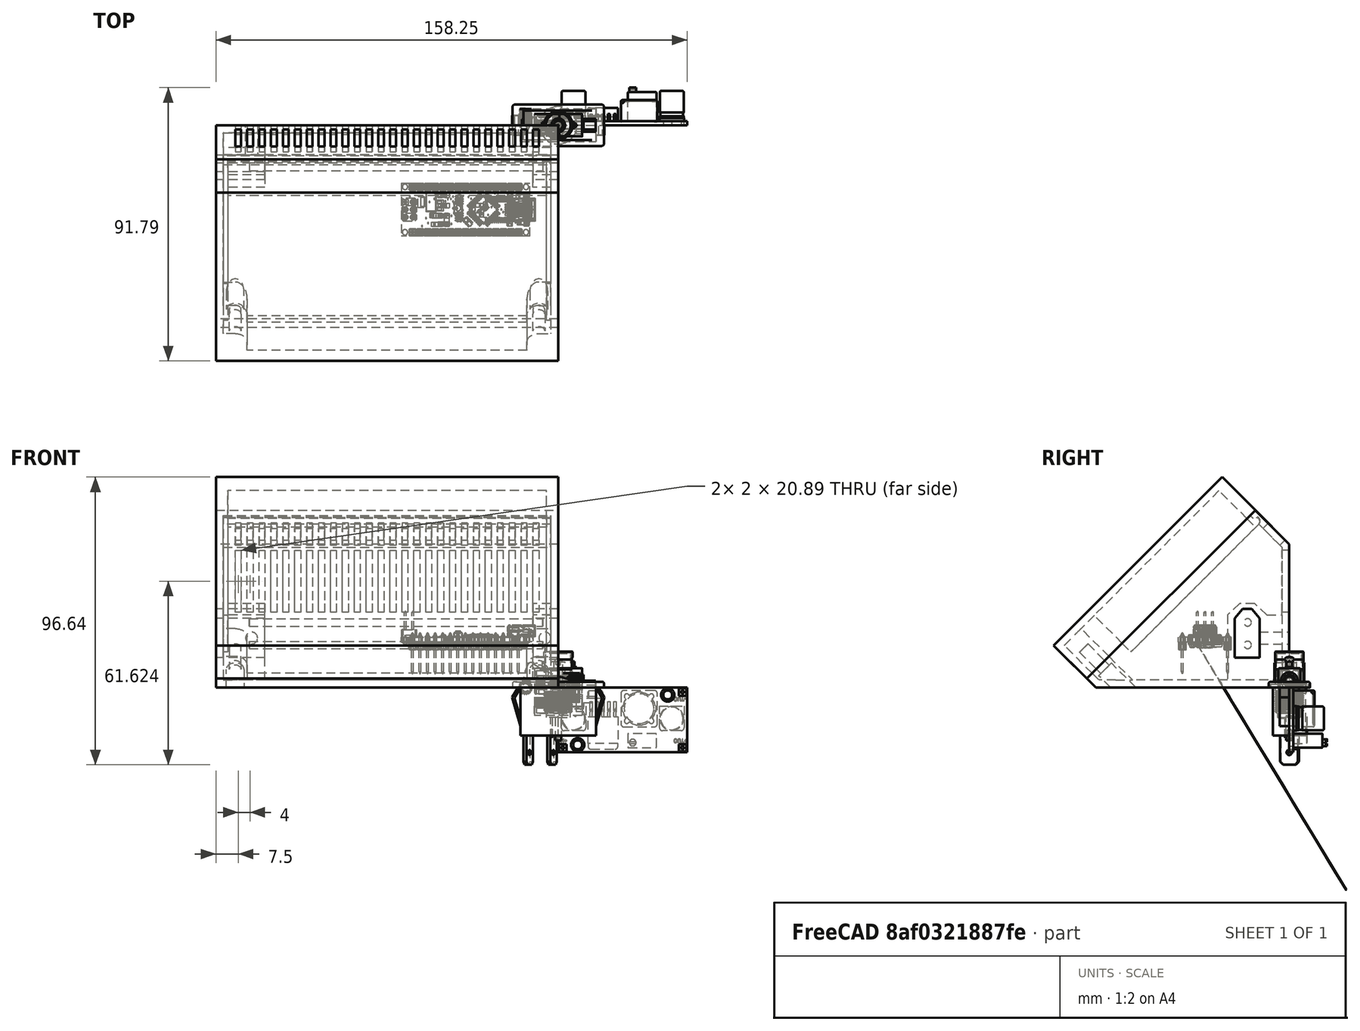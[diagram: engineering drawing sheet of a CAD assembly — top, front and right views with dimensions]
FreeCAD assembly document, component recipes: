
FREECAD ASSEMBLY — COMPONENT RECIPES ("genFonc_005_surBase35mm_008.1")

This assembly document has 17 components, labeled P0..P16 below (a component is one placed body or linked part). 10 of them carry a construction recipe — the FreeCAD feature program that regenerates the part from scratch, quoted from this document or its linked companion documents; the rest are supplied as boundary geometry only. No exploded tour is included for this assembly.
COMPONENT P0 — recipe-attached ("base", modeled in this document).
Construction recipe (the document's own serialized feature program — sketch geometry with constraints, then the solid features built on it; lengths are millimeters unless a unit is written):

FEATURE [PartDesign::FeatureBase] Clone
  BaseFeature = -> Slice_child0
FEATURE [PartDesign::Thickness] Thickness
  Base = -> Clone [Face7]
  BaseFeature = -> Clone
  Intersection = false
  Join = 0
  Mode = 0
  Reversed = true
  SupportTransform = false
  Value = 2.5
  expr: Value = <<sp>>.epaisseurParois
FEATURE [PartDesign::Plane] DatumPlane001  label="planXt"
  AttachmentOffset = pos=(0,0,-2.5) rot=(0,0,1;0rad)
  Length = 110.737
  MapMode = 5
  Placement = pos=(-2.5,6e-16,-6e-16) rot=(0.57735,0.57735,0.57735;2.0944rad)
  ResizeMode = 0
  Support = -> [YZ_Plane002]
  Width = 102.305
  expr: .AttachmentOffset.Base.z = -<<sp>>.epaisseurParois
FEATURE [Sketcher::SketchObject] Sketch002  label="sk_renfortXt"
  FullyConstrained = true
  MapMode = 5
  Placement = pos=(-2.5,6e-16,-6e-16) rot=(0.57735,0.57735,0.57735;2.0944rad)
  Support = -> [DatumPlane001]
  expr: Constraints[13] = <<sp>>.xt60largeurFetiere
  expr: Constraints[16] = <<sp>>.xt60base
  expr: Constraints[14] = <<sp>>.xt60hauteur
  expr: Constraints[18] = .Constraints.dist
  expr: Constraints[34] = .Constraints.epRf
  expr: .Constraints.epRf = <<sp>>.xt60epRenfort
  expr: Constraints[15] = <<sp>>.xt60hauteurToit
  expr: Constraints[45] = <<sp>>.epaisseurParois
  expr: .Constraints.dist = <<sp>>.xt60distanceAngleBord
  expr: Constraints[31] = <<sp>>.epaisseurParois
  expr: Constraints[32] = .Constraints.epRf
  sketch-geometry (17):
    g0: LineSegment StartX=-18.3 StartY=10 StartZ=0 EndX=-18.3 EndY=23.25 EndZ=0
    g1: LineSegment StartX=-18.3 StartY=23.25 StartZ=0 EndX=-15.65 EndY=25.75 EndZ=0
    g2: LineSegment StartX=-15.65 StartY=25.75 StartZ=0 EndX=-12.65 EndY=25.75 EndZ=0
    g3: LineSegment StartX=-12.65 StartY=25.75 StartZ=0 EndX=-10 EndY=23.25 EndZ=0
    g4: LineSegment StartX=-10 StartY=23.25 StartZ=0 EndX=-10 EndY=10 EndZ=0
    g5: LineSegment StartX=-10 StartY=10 StartZ=0 EndX=-18.3 EndY=10 EndZ=0
    g6: LineSegment StartX=-14.15 StartY=10 StartZ=0 EndX=-14.15 EndY=25.75 EndZ=0
    g7: LineSegment StartX=-16.6431 StartY=28.25 StartZ=0 EndX=-20.8 EndY=24.3284 EndZ=0
    g8: LineSegment StartX=-20.8 StartY=24.3284 StartZ=0 EndX=-20.8 EndY=2.5 EndZ=0
    g9: LineSegment StartX=-20.8 StartY=2.5 StartZ=0 EndX=-7.5 EndY=2.5 EndZ=0
    g10: LineSegment StartX=-7.5 StartY=2.5 StartZ=0 EndX=-7.5 EndY=24.3284 EndZ=0
    g11: LineSegment StartX=-7.5 StartY=24.3284 StartZ=0 EndX=-11.6569 EndY=28.25 EndZ=0
    g12: LineSegment StartX=-11.6569 StartY=28.25 StartZ=0 EndX=-16.6431 EndY=28.25 EndZ=0
    g13: LineSegment StartX=-7.5 StartY=24.3284 StartZ=0 EndX=-2.5 EndY=24.3284 EndZ=0
    g14: LineSegment StartX=-2.5 StartY=24.3284 StartZ=0 EndX=-2.5 EndY=2.5 EndZ=0
    g15: LineSegment StartX=-2.5 StartY=2.5 StartZ=0 EndX=-7.5 EndY=2.5 EndZ=0
    g16: LineSegment StartX=-7.5 StartY=2.5 StartZ=0 EndX=-7.5 EndY=24.3284 EndZ=0
  constraints (46):
    c: Vertical(g0)
    c: Coincident(g0,g1)
    c: Coincident(g1,g2)
    c: Horizontal(g2)
    c: Coincident(g2,g3)
    c: Coincident(g3,g4)
    c: Vertical(g4)
    c: Coincident(g4,g5)
    c: Coincident(g5,g0)
    c: Horizontal(g5)
    c: Symmetric(g1,g2,g6)
    c: Equal(g0,g4)
    c: Symmetric(g0,g4,g6)
    c: DistanceX(g2,g2) = 3
    c: DistanceY(g4,g4) = 13.25
    c: DistanceY(g3,g2) = 2.5
    c: DistanceX(g5,g5) = 8.3
    c: DistanceX(g4,g-1) = 10  'dist'
    c: DistanceY(g-1,g4) = 10
    c: Coincident(g7,g8)
    c: Vertical(g8)
    c: Coincident(g8,g9)
    c: Horizontal(g9)
    c: Coincident(g9,g10)
    c: Coincident(g10,g11)
    c: Coincident(g11,g12)
    c: Coincident(g12,g7)
    c: Symmetric(g7,g10,g6)
    c: Symmetric(g7,g11,g6)
    c: Symmetric(g8,g9,g6)
    c: DistanceX(g8,g0) = 2.5  'epRf'
    c: DistanceY(g-1,g9) = 2.5
    c: Distance(g7,g1) = 2.5
    c: Parallel(g1,g7)
    c: DistanceY(g2,g11) = 2.5
    c: Coincident(g13,g14)
    c: Coincident(g14,g15)
    c: Coincident(g15,g16)
    c: Coincident(g16,g13)
    c: Horizontal(g13)
    c: Horizontal(g15)
    c: Vertical(g14)
    c: Vertical(g16)
    c: Coincident(g13,g11)
    c: Horizontal(g14,g9)
    c: DistanceX(g14,g-1) = 2.5
FEATURE [PartDesign::Pad] Pad001  label="renfortXt"
  AllowMultiFace = false
  BaseFeature = -> Thickness
  Direction = (1,1,1)
  Length = 110
  Length2 = 100
  Profile = -> Sketch002
  Reversed = true
  Type = 0
  expr: Length = <<sp>>.largeurModuleBase - 2 * <<sp>>.epaisseurParois
FEATURE [Sketcher::SketchObject] Sketch003  label="sk_trouXt"
  FullyConstrained = true
  MapMode = 5
  Placement = pos=(0,0,0) rot=(0.57735,0.57735,0.57735;2.0944rad)
  Support = -> [YZ_Plane002]
  expr: Constraints[14] = <<sp>>.xt60hauteur
  expr: .Constraints.dist = <<sp>>.xt60distanceAngleBord
  expr: Constraints[15] = <<sp>>.xt60hauteurToit + <<sp>>.xtJeu
  expr: Constraints[16] = <<sp>>.xt60largeurFetiere
  expr: Constraints[13] = <<sp>>.xt60base
  expr: Constraints[18] = .Constraints.dist
  sketch-geometry (7):
    g0: LineSegment StartX=-18.3 StartY=10 StartZ=0 EndX=-18.3 EndY=23.25 EndZ=0
    g1: LineSegment StartX=-18.3 StartY=23.25 StartZ=0 EndX=-15.65 EndY=26.35 EndZ=0
    g2: LineSegment StartX=-15.65 StartY=26.35 StartZ=0 EndX=-12.65 EndY=26.35 EndZ=0
    g3: LineSegment StartX=-12.65 StartY=26.35 StartZ=0 EndX=-10 EndY=23.25 EndZ=0
    g4: LineSegment StartX=-10 StartY=23.25 StartZ=0 EndX=-10 EndY=10 EndZ=0
    g5: LineSegment StartX=-10 StartY=10 StartZ=0 EndX=-18.3 EndY=10 EndZ=0
    g6: LineSegment StartX=-14.15 StartY=10 StartZ=0 EndX=-14.15 EndY=26.35 EndZ=0
  constraints (19):
    c: Vertical(g0)
    c: Coincident(g0,g1)
    c: Coincident(g1,g2)
    c: Horizontal(g2)
    c: Coincident(g2,g3)
    c: Coincident(g3,g4)
    c: Coincident(g4,g5)
    c: Coincident(g5,g0)
    c: Horizontal(g5)
    c: Symmetric(g1,g2,g6)
    c: Symmetric(g0,g3,g6)
    c: Vertical(g6)
    c: Symmetric(g0,g4,g6)
    c: DistanceX(g5,g5) = 8.3
    c: DistanceY(g4,g4) = 13.25
    c: DistanceY(g3,g2) = 3.1
    c: DistanceX(g2,g2) = 3
    c: DistanceX(g4,g-1) = 10  'dist'
    c: DistanceY(g-1,g4) = 10
FEATURE [PartDesign::Pocket] Pocket
  AllowMultiFace = false
  BaseFeature = -> Pad001
  Length = 115
  Length2 = 100
  Profile = -> Sketch003
  Type = 0
  expr: Length = <<sp>>.largeurModuleBase
FEATURE [PartDesign::Plane] DatumPlane002  label="planDecoupeRenfortXt"
  AttachmentOffset = pos=(0,0,2.5) rot=(0,0,1;0rad)
  Length = 161.762
  MapMode = 5
  Placement = pos=(0,-2.5,-6e-16) rot=(1,0,0;1.5708rad)
  ResizeMode = 0
  Support = -> [XZ_Plane002]
  Width = 106.331
  expr: .AttachmentOffset.Base.z = <<sp>>.epaisseurParois
FEATURE [Sketcher::SketchObject] Sketch004  label="sk_decoupRenfXt"
  FullyConstrained = true
  MapMode = 5
  Placement = pos=(0,-2.5,-6e-16) rot=(1,0,0;1.5708rad)
  Support = -> [DatumPlane002]
  expr: Constraints[8] = <<sp>>.epaisseurParois
  expr: Constraints[9] = <<sp>>.xt60distanceAngleBord + <<sp>>.xt60hauteur + <<sp>>.xt60hauteurToit + <<sp>>.xt60epRenfort
  expr: Constraints[10] = <<sp>>.xt60LongueurRenfortPetit + <<sp>>.epaisseurParois
  expr: Constraints[11] = <<sp>>.largeurModuleBase - (<<sp>>.xt60longueurRenfortGrand + <<sp>>.epaisseurParois)
  sketch-geometry (4):
    g0: LineSegment StartX=-98.5 StartY=28.25 StartZ=0 EndX=-8.5 EndY=28.25 EndZ=0
    g1: LineSegment StartX=-8.5 StartY=28.25 StartZ=0 EndX=-8.5 EndY=2.5 EndZ=0
    g2: LineSegment StartX=-8.5 StartY=2.5 StartZ=0 EndX=-98.5 EndY=2.5 EndZ=0
    g3: LineSegment StartX=-98.5 StartY=2.5 StartZ=0 EndX=-98.5 EndY=28.25 EndZ=0
  constraints (12):
    c: Coincident(g0,g1)
    c: Coincident(g1,g2)
    c: Coincident(g2,g3)
    c: Coincident(g3,g0)
    c: Horizontal(g0)
    c: Horizontal(g2)
    c: Vertical(g1)
    c: Vertical(g3)
    c: DistanceY(g-1,g1) = 2.5
    c: DistanceY(g-1,g0) = 28.25
    c: DistanceX(g1,g-1) = 8.5
    c: DistanceX(g2,g-1) = 98.5
FEATURE [PartDesign::Pocket] Pocket001  label="decoupeRenfXt"
  AllowMultiFace = false
  BaseFeature = -> Pocket
  Length = 23.3
  Length2 = 100
  Profile = -> Sketch004
  Reversed = true
  Type = 0
  expr: Length = <<sp>>.xt60distanceAngleBord + <<sp>>.xt60base + 2 * <<sp>>.xt60epRenfort
FEATURE [Sketcher::SketchObject] Sketch005  label="xt60PercagePostMale"
  FullyConstrained = true
  MapMode = 5
  Placement = pos=(0,0,0) rot=(1,0,0;1.5708rad)
  Support = -> [XZ_Plane002]
  expr: Constraints[0] = <<sp>>.insertDiamPercage
  expr: Constraints[1] = <<sp>>.insertDistanceTrouBordMale
  expr: Constraints[2] = <<sp>>.insertHauteur
  sketch-geometry (1):
    g0: Circle CenterX=-4.5 CenterY=16.625 CenterZ=0 NormalX=0 NormalY=0 NormalZ=1 AngleXU=0 Radius=2
  constraints (3):
    c: Diameter(g0) = 4
    c: DistanceX(g0,g-1) = 4.5
    c: DistanceY(g-1,g0) = 16.625
FEATURE [PartDesign::Pocket] Pocket002  label="insertXtMale"
  AllowMultiFace = false
  BaseFeature = -> Pocket001
  Length = 10
  Length2 = 100
  Profile = -> Sketch005
  Reversed = true
  Type = 0
  expr: Length = <<sp>>.insertProfondeurPercage
FEATURE [Sketcher::SketchObject] Sketch006  label="xt60PercagePostFem"
  FullyConstrained = true
  MapMode = 5
  Placement = pos=(0,0,0) rot=(1,0,0;1.5708rad)
  Support = -> [XZ_Plane002]
  expr: Constraints[0] = <<sp>>.insertDiamPercage
  expr: Constraints[1] = <<sp>>.insertDistanceTrouBordFem
  expr: Constraints[2] = <<sp>>.insertHauteur
  sketch-geometry (1):
    g0: Circle CenterX=-103 CenterY=16.625 CenterZ=0 NormalX=0 NormalY=0 NormalZ=1 AngleXU=0 Radius=2
  constraints (3):
    c: Diameter(g0) = 4
    c: DistanceX(g0,g-1) = 103
    c: DistanceY(g-1,g0) = 16.625
FEATURE [PartDesign::Pocket] Pocket003  label="insertXt60Fem"
  AllowMultiFace = false
  BaseFeature = -> Pocket002
  Length = 10
  Length2 = 100
  Profile = -> Sketch006
  Reversed = true
  Type = 0
  expr: Length = <<sp>>.insertProfondeurPercage
FEATURE [PartDesign::Plane] DatumPlane003
  AttachmentOffset = pos=(0,0,2.5) rot=(0,0,1;0rad)
  Length = 162.821
  MapMode = 2
  Placement = pos=(0,0,2.5) rot=(0,0,1;0rad)
  ResizeMode = 0
  Support = -> [XY_Plane002]
  Width = 115.821
  expr: .AttachmentOffset.Base.z = <<sp>>.epaisseurParois
FEATURE [PartDesign::Plane] DatumPlane004  label="planTrancheur"
  AttachmentOffset = pos=(0,0,71) rot=(-1,0,0;0.785398rad)
  Length = 166.517
  MapMode = 5
  Placement = pos=(0,-71,-1.58e-14) rot=(1,0,0;0.785398rad)
  ResizeMode = 0
  Support = -> [XZ_Plane002]
  Width = 152.077
  expr: .AttachmentOffset.Base.z = <<sp>>.planTrancheur
FEATURE [Sketcher::SketchObject] Sketch008
  FullyConstrained = true
  MapMode = 5
  Placement = pos=(0,-71,-2.13e-14) rot=(1,0,0;0.785398rad)
  Support = -> [DatumPlane004]
  expr: Constraints[1] = <<sp>>.insertFavDistAuZeroDuPLan
  expr: Constraints[13] = <<sp>>.epaisseurParois
  expr: Constraints[16] = <<sp>>.insertDiamPercage / 2 + <<sp>>.insertFAVMargeDist
  expr: .Constraints.dist = <<sp>>.epaisseurParois
  expr: Constraints[21] = <<sp>>.insertFAVDistBord
  expr: Constraints[22] = <<sp>>.largeurModuleBase - <<sp>>.epaisseurParois
  sketch-geometry (7):
    g0: LineSegment StartX=-2.5 StartY=4.24264 StartZ=0 EndX=-112.5 EndY=4.24264 EndZ=0
    g1: LineSegment StartX=-6.5 StartY=14.7426 StartZ=0 EndX=-2.5 EndY=14.7426 EndZ=0
    g2: LineSegment StartX=-2.5 StartY=14.7426 StartZ=0 EndX=-2.5 EndY=6.74264 EndZ=0
    g3: LineSegment StartX=-2.5 StartY=6.74264 StartZ=0 EndX=-10.5 EndY=6.74264 EndZ=0
    g4: LineSegment StartX=-10.5 StartY=6.74264 StartZ=0 EndX=-10.5 EndY=10.7426 EndZ=0
    g5: ArcOfCircle CenterX=-6.5 CenterY=10.7426 CenterZ=0 NormalX=0 NormalY=0 NormalZ=1 AngleXU=0 Radius=4 StartAngle=1.5708 EndAngle=3.14159
    g6: LineSegment StartX=-6.5 StartY=10.7426 StartZ=0 EndX=-6.5 EndY=6.74264 EndZ=0
  constraints (23):
    c: Horizontal(g0)
    c: DistanceY(g-1,g0) = 4.24264
    c: DistanceX(g0,g-1) = 2.5  'dist'
    c: Horizontal(g1)
    c: Coincident(g1,g2)
    c: Vertical(g2)
    c: Coincident(g2,g3)
    c: Horizontal(g3)
    c: Coincident(g3,g4)
    c: Vertical(g4)
    c: Vertical(g2,g0)
    c: Equal(g3,g2)
    c: Equal(g4,g1)
    c: DistanceY(g0,g2) = 2.5
    c: Coincident(g5,g4)
    c: Coincident(g5,g1)
    c: DistanceX(g5,g2) = 4
    c: Coincident(g6,g5)
    c: PointOnObject(g6,g3)
    c: Vertical(g6)
    c: Vertical(g5,g1)
    c: DistanceX(g3,g3) = 8
    c: DistanceX(g0,g-1) = 112.5
FEATURE [PartDesign::Pad] Pad003  label="padTrouFAVDroite"
  AllowMultiFace = false
  BaseFeature = -> Pocket003
  Direction = (1,1,1)
  Length = 10
  Length2 = 100
  Profile = -> Sketch008
  Reversed = true
  Type = 3
  UpToFace = -> DatumPlane003
FEATURE [Sketcher::SketchObject] Sketch009
  FullyConstrained = true
  MapMode = 5
  Placement = pos=(0,-71,-2.13e-14) rot=(1,0,0;0.785398rad)
  Support = -> [DatumPlane004]
  expr: .Constraints.larg = <<sp>>.insertFAVDistBord
  expr: Constraints[8] = .Constraints.larg
  expr: Constraints[11] = .Constraints.larg / 2
  expr: Constraints[12] = <<sp>>.largeurModuleBase
  expr: Constraints[13] = <<sp>>.insertFavDistAuZeroDuPLan
  expr: Constraints[14] = <<sp>>.epaisseurParois
  expr: Constraints[15] = <<sp>>.epaisseurParois
  sketch-geometry (6):
    g0: LineSegment StartX=-112.5 StartY=6.74264 StartZ=0 EndX=-104.5 EndY=6.74264 EndZ=0
    g1: LineSegment StartX=-104.5 StartY=6.74264 StartZ=0 EndX=-104.5 EndY=10.7426 EndZ=0
    g2: LineSegment StartX=-108.5 StartY=14.7426 StartZ=0 EndX=-112.5 EndY=14.7426 EndZ=0
    g3: LineSegment StartX=-112.5 StartY=14.7426 StartZ=0 EndX=-112.5 EndY=6.74264 EndZ=0
    g4: ArcOfCircle CenterX=-108.5 CenterY=10.7426 CenterZ=0 NormalX=0 NormalY=0 NormalZ=1 AngleXU=0 Radius=4 StartAngle=0 EndAngle=1.5708
    g5: GeomPoint X=-115 Y=4.24264 Z=0
  constraints (16):
    c: Coincident(g0,g1)
    c: Coincident(g2,g3)
    c: Coincident(g3,g0)
    c: Horizontal(g0)
    c: Horizontal(g2)
    c: Vertical(g1)
    c: Vertical(g3)
    c: DistanceX(g0,g0) = 8  'larg'
    c: DistanceY(g3,g3) = 8
    c: Tangent(g2,g4) = -1.5708
    c: Tangent(g1,g4) = -1.5708
    c: DistanceX(g0,g4) = 4
    c: DistanceX(g5,g-1) = 115
    c: DistanceY(g-1,g5) = 4.24264
    c: DistanceX(g5,g0) = 2.5
    c: DistanceY(g5,g0) = 2.5
FEATURE [PartDesign::Pad] Pad004  label="padTrouFavGauche"
  AllowMultiFace = false
  BaseFeature = -> Pad003
  Direction = (1,1,1)
  Length = 10
  Length2 = 100
  Profile = -> Sketch009
  Type = 3
  UpToFace = -> DatumPlane003 [Plane]
FEATURE [Sketcher::SketchObject] Sketch010
  FullyConstrained = true
  MapMode = 5
  Placement = pos=(0,-71,-2.13e-14) rot=(1,0,0;0.785398rad)
  Support = -> [DatumPlane004]
  expr: Constraints[0] = <<sp>>.insertFAVDistBord / 2 + <<sp>>.epaisseurParois
  expr: Constraints[1] = <<sp>>.insertFavDistAuZeroDuPLan + <<sp>>.epaisseurParois + <<sp>>.insertFAVDistBord / 2
  expr: Constraints[2] = <<sp>>.insertDiamPercage
  sketch-geometry (1):
    g0: Circle CenterX=-6.5 CenterY=10.7426 CenterZ=0 NormalX=0 NormalY=0 NormalZ=1 AngleXU=0 Radius=2
  constraints (3):
    c: DistanceX(g0,g-1) = 6.5
    c: DistanceY(g-1,g0) = 10.7426
    c: Diameter(g0) = 4
FEATURE [PartDesign::Pocket] Pocket004  label="trouDroit"
  AllowMultiFace = false
  BaseFeature = -> Pad004
  Length = 5
  Length2 = 100
  Profile = -> Sketch010
  Type = 1
FEATURE [Sketcher::SketchObject] Sketch011
  FullyConstrained = true
  MapMode = 5
  Placement = pos=(0,-71,-2.13e-14) rot=(1,0,0;0.785398rad)
  Support = -> [DatumPlane004]
  expr: Constraints[0] = <<sp>>.insertDiamPercage
  expr: Constraints[1] = <<sp>>.largeurModuleBase - <<sp>>.epaisseurParois - <<sp>>.insertFAVDistBord / 2
  expr: Constraints[2] = <<sp>>.insertFavDistAuZeroDuPLan + <<sp>>.epaisseurParois + <<sp>>.insertFAVDistBord / 2
  sketch-geometry (1):
    g0: Circle CenterX=-108.5 CenterY=10.7426 CenterZ=0 NormalX=0 NormalY=0 NormalZ=1 AngleXU=0 Radius=2
  constraints (3):
    c: Diameter(g0) = 4
    c: DistanceX(g0,g-1) = 108.5
    c: DistanceY(g-1,g0) = 10.7426
FEATURE [PartDesign::Pocket] Pocket005  label="trouGauche"
  AllowMultiFace = false
  BaseFeature = -> Pocket004
  Length = 5
  Length2 = 100
  Profile = -> Sketch011
  Type = 1
FEATURE [PartDesign::Plane] DatumPlane005  label="planTeteVisFav"
  AttachmentOffset = pos=(0,0,68) rot=(-1,0,0;0.785398rad)
  Length = 166.517
  MapMode = 5
  Placement = pos=(0,-68,-1.51e-14) rot=(1,0,0;0.785398rad)
  ResizeMode = 0
  Support = -> [XZ_Plane002]
  Width = 152.077
  expr: .AttachmentOffset.Base.z = <<sp>>.planTrancheur - 3
FEATURE [Sketcher::SketchObject] Sketch012
  ExternalGeometry = -> [Pocket005]
  FullyConstrained = true
  MapMode = 5
  Placement = pos=(0,-68,-1.42e-14) rot=(1,0,0;0.785398rad)
  Support = -> [DatumPlane005]
  expr: Constraints[1] = <<sp>>.visM3DiamEncastrement
  sketch-geometry (2):
    g0: Circle CenterX=-6.5 CenterY=8.62132 CenterZ=0 NormalX=0 NormalY=0 NormalZ=1 AngleXU=0 Radius=3
    g1: Circle CenterX=-108.5 CenterY=8.62132 CenterZ=0 NormalX=0 NormalY=0 NormalZ=1 AngleXU=0 Radius=3
  constraints (4):
    c: Equal(g0,g1)
    c: Diameter(g1) = 6
    c: Coincident(g1,g-4)
    c: Coincident(g-3,g0)
FEATURE [PartDesign::Pocket] Pocket006  label="evidementTeteVisFav"
  AllowMultiFace = false
  BaseFeature = -> Pocket005
  Length = 20
  Length2 = 100
  Profile = -> Sketch012
  Type = 1
FEATURE [Sketcher::SketchObject] Sketch014
  FullyConstrained = true
  MapMode = 5
  Placement = pos=(0,0,0) rot=(1,0,0;1.5708rad)
  Support = -> [XZ_Plane002]
  expr: Constraints[2] = <<sp>>.hauteurDuDos
  expr: Constraints[3] = <<sp>>.largeurModuleBase / 2
  expr: Constraints[12] = <<sp>>.xt60distanceAngleBord + <<sp>>.xt60hauteur + <<sp>>.ventilDistBordFente
  expr: Constraints[13] = <<sp>>.ventilLargeurFentes
  expr: Constraints[14] = <<sp>>.ventilEcartfente / 2
  expr: Constraints[15] = <<sp>>.hauteurDuDos - <<sp>>.ventilDistBordFente
  sketch-geometry (5):
    g0: LineSegment StartX=-57.5 StartY=0 StartZ=0 EndX=-57.5 EndY=48.1371 EndZ=0
    g1: LineSegment StartX=-60.5 StartY=46.1371 StartZ=0 EndX=-58.5 EndY=46.1371 EndZ=0
    g2: LineSegment StartX=-58.5 StartY=46.1371 StartZ=0 EndX=-58.5 EndY=25.25 EndZ=0
    g3: LineSegment StartX=-58.5 StartY=25.25 StartZ=0 EndX=-60.5 EndY=25.25 EndZ=0
    g4: LineSegment StartX=-60.5 StartY=25.25 StartZ=0 EndX=-60.5 EndY=46.1371 EndZ=0
  constraints (16):
    c: PointOnObject(g0,g-1)
    c: Vertical(g0)
    c: DistanceY(g0,g0) = 48.1371
    c: DistanceX(g0,g-1) = 57.5
    c: Coincident(g1,g2)
    c: Coincident(g2,g3)
    c: Coincident(g3,g4)
    c: Coincident(g4,g1)
    c: Horizontal(g1)
    c: Horizontal(g3)
    c: Vertical(g2)
    c: Vertical(g4)
    c: DistanceY(g-1,g2) = 25.25
    c: DistanceX(g1,g1) = 2
    c: DistanceX(g2,g0) = 1
    c: DistanceY(g-1,g1) = 46.1371
FEATURE [PartDesign::Pocket] Pocket008  label="ventilFente1"
  AllowMultiFace = false
  BaseFeature = -> Pocket006
  Length = 2.5
  Length2 = 100
  Profile = -> Sketch014
  Reversed = true
  Type = 0
  expr: Length = <<sp>>.epaisseurParois
FEATURE [PartDesign::LinearPattern] LinearPattern  label="ventilDosRepeat1"
  BaseFeature = -> Pocket008
  Direction = -> Sketch014 [H_Axis]
  Length = 48
  Occurrences = 13
  Originals = -> [Pocket008]
  Reversed = true
  expr: Length = <<sp>>.ventilLargeurRepet
  expr: Occurrences = <<sp>>.ventilNbrFents
FEATURE [PartDesign::LinearPattern] LinearPattern001  label="ventilDosRepeat2"
  BaseFeature = -> LinearPattern
  Direction = -> Sketch014 [H_Axis]
  Length = 52
  Occurrences = 14
  Originals = -> [Pocket008]
  expr: Length = <<sp>>.ventilLargeurRepet + <<sp>>.ventilEcartfente + <<sp>>.ventilLargeurFentes
  expr: Occurrences = <<sp>>.ventilNbrFents + 1
FEATURE [PartDesign::Plane] DatumPlane006  label="planVentilSup"
  AttachmentOffset = pos=(0,0,-48.1371) rot=(1,0,0;0.785398rad)
  Length = 166.517
  MapMode = 5
  Placement = pos=(0,48.1371,1.07e-14) rot=(1,0,0;2.35619rad)
  ResizeMode = 0
  Support = -> [XZ_Plane002]
  Width = 152.077
  expr: .AttachmentOffset.Base.z = -<<sp>>.hauteurDuDos
FEATURE [Sketcher::SketchObject] Sketch015
  FullyConstrained = true
  MapMode = 5
  Placement = pos=(0,48.1371,1.07e-14) rot=(1,0,0;2.35619rad)
  Support = -> [DatumPlane006]
  expr: Constraints[8] = <<sp>>.distanceAuZeroPlanBorArriere + <<sp>>.ventilDistBordFente
  expr: Constraints[10] = <<sp>>.ventilLargeurFentes
  expr: Constraints[11] = (<<sp>>.largeurModuleBase + <<sp>>.ventilEcartfente) / 2
  expr: Constraints[9] = <<sp>>.longPetitRetSupSansFav - 2 * <<sp>>.ventilDistBordFente - <<sp>>.favBordureProf
  sketch-geometry (4):
    g0: LineSegment StartX=-58.5 StartY=78.0926 StartZ=0 EndX=-60.5 EndY=78.0926 EndZ=0
    g1: LineSegment StartX=-60.5 StartY=78.0926 StartZ=0 EndX=-60.5 EndY=70.0761 EndZ=0
    g2: LineSegment StartX=-60.5 StartY=70.0761 StartZ=0 EndX=-58.5 EndY=70.0761 EndZ=0
    g3: LineSegment StartX=-58.5 StartY=70.0761 StartZ=0 EndX=-58.5 EndY=78.0926 EndZ=0
  constraints (12):
    c: Coincident(g0,g1)
    c: Coincident(g1,g2)
    c: Coincident(g2,g3)
    c: Coincident(g3,g0)
    c: Horizontal(g0)
    c: Horizontal(g2)
    c: Vertical(g1)
    c: Vertical(g3)
    c: DistanceY(g-1,g2) = 70.0761
    c: DistanceY(g2,g0) = 8.01652
    c: DistanceX(g0,g0) = 2
    c: DistanceX(g2,g-1) = 58.5
FEATURE [PartDesign::Pocket] Pocket009  label="ventilSupFente"
  AllowMultiFace = false
  BaseFeature = -> LinearPattern001
  Length = 5
  Length2 = 100
  Profile = -> Sketch015
  Reversed = true
  Type = 0
FEATURE [PartDesign::LinearPattern] LinearPattern002  label="ventilSupRepeat1"
  BaseFeature = -> Pocket009
  Direction = -> Sketch015 [H_Axis]
  Length = 48
  Occurrences = 13
  Originals = -> [Pocket009]
  Reversed = true
  expr: Length = <<sp>>.ventilLargeurRepet
  expr: Occurrences = <<sp>>.ventilNbrFents
FEATURE [PartDesign::LinearPattern] LinearPattern003  label="ventilSupRepeat2"
  BaseFeature = -> LinearPattern002
  Direction = -> Sketch015 [H_Axis]
  Length = 52
  Occurrences = 14
  Originals = -> [Pocket009]
  expr: Length = <<sp>>.ventilLargeurRepet + <<sp>>.ventilEcartfente + <<sp>>.ventilLargeurFentes
  expr: Occurrences = <<sp>>.ventilNbrFents + 1
FEATURE [PartDesign::Body] Body001  label="base"
  BaseFeature = -> Slice_child0
  Group = -> [Clone,Thickness,DatumPlane001,Sketch002,Pad001,Sketch003,Pocket,DatumPlane002,Sketch004,Pocket001,Sketch005,Pocket002,Sketch006,Pocket003,DatumPlane003,DatumPlane004,Sketch008,Pad003,Sketch009,Pad004,Sketch010,Pocket004,Sketch011,Pocket005,DatumPlane005,Sketch012,Pocket006,Sketch014,Pocket008,LinearPattern,LinearPattern001,DatumPlane006,Sketch015,Pocket009,LinearPattern002,LinearPattern003,+3 more]
  Origin = -> Origin002
  Tip = -> Pocket015
COMPONENT P1 — recipe-attached ("faceAvant", modeled in this document).
Construction recipe (the document's own serialized feature program — sketch geometry with constraints, then the solid features built on it; lengths are millimeters unless a unit is written):

FEATURE [PartDesign::FeatureBase] Clone001
  BaseFeature = -> Slice_child1
FEATURE [PartDesign::Thickness] Thickness001
  Base = -> Clone001 [Face5]
  BaseFeature = -> Clone001
  Intersection = false
  Join = 0
  Mode = 0
  Reversed = true
  SupportTransform = false
  Value = 2.5
  expr: Value = <<sp>>.epaisseurParois
FEATURE [PartDesign::Plane] DatumPlane007  label="planTrancheurBis"
  AttachmentOffset = pos=(0,0,71) rot=(-1,0,0;0.785398rad)
  Length = 168.138
  MapMode = 5
  Placement = pos=(0,-71,-1.58e-14) rot=(1,0,0;0.785398rad)
  ResizeMode = 0
  Support = -> [XZ_Plane003]
  Width = 169.523
  expr: .AttachmentOffset.Base.z = <<sp>>.planTrancheur
FEATURE [Sketcher::SketchObject] Sketch016  label="sk_insertFavDroit"
  FullyConstrained = true
  MapMode = 5
  Placement = pos=(0,-71,-2.13e-14) rot=(1,0,0;0.785398rad)
  Support = -> [DatumPlane007]
  expr: Constraints[7] = <<sp>>.epaisseurParois
  expr: Constraints[8] = <<sp>>.insertFavDistAuZeroDuPLan + <<sp>>.epaisseurParois
  expr: Constraints[9] = <<sp>>.insertFAVDistBord
  expr: Constraints[14] = <<sp>>.insertFAVDistBord / 2
  expr: Constraints[11] = <<sp>>.insertFAVDistBord
  sketch-geometry (5):
    g0: LineSegment StartX=-6.5 StartY=14.7426 StartZ=0 EndX=-2.5 EndY=14.7426 EndZ=0
    g1: LineSegment StartX=-2.5 StartY=14.7426 StartZ=0 EndX=-2.5 EndY=6.74264 EndZ=0
    g2: LineSegment StartX=-2.5 StartY=6.74264 StartZ=0 EndX=-10.5 EndY=6.74264 EndZ=0
    g3: LineSegment StartX=-10.5 StartY=6.74264 StartZ=0 EndX=-10.5 EndY=10.7426 EndZ=0
    g4: ArcOfCircle CenterX=-6.5 CenterY=10.7426 CenterZ=0 NormalX=0 NormalY=0 NormalZ=1 AngleXU=0 Radius=4 StartAngle=1.5708 EndAngle=3.14159
  constraints (15):
    c: Horizontal(g0)
    c: Coincident(g0,g1)
    c: Vertical(g1)
    c: Coincident(g1,g2)
    c: Horizontal(g2)
    c: Coincident(g2,g3)
    c: Vertical(g3)
    c: DistanceX(g1,g-1) = 2.5
    c: DistanceY(g-1,g1) = 6.74264
    c: DistanceY(g1,g1) = 8
    c: Equal(g3,g0)
    c: DistanceX(g2,g2) = 8
    c: Coincident(g4,g0)
    c: Tangent(g4,g3) = 1.5708
    c: DistanceX(g4,g1) = 4
FEATURE [PartDesign::Pad] Pad005  label="padInsertFavDroit"
  AllowMultiFace = false
  BaseFeature = -> Thickness001
  Direction = (1,1,1)
  Length = 10
  Length2 = 100
  Profile = -> Sketch016
  Type = 2
FEATURE [Sketcher::SketchObject] Sketch017  label="sp_padInserFavGauch"
  FullyConstrained = true
  MapMode = 5
  Placement = pos=(0,-71,-2.13e-14) rot=(1,0,0;0.785398rad)
  Support = -> [DatumPlane007]
  expr: Constraints[12] = <<sp>>.insertFAVDistBord / 2
  expr: Constraints[10] = <<sp>>.insertFAVDistBord
  expr: Constraints[13] = <<sp>>.largeurModuleBase
  expr: Constraints[14] = <<sp>>.insertFavDistAuZeroDuPLan
  expr: Constraints[15] = <<sp>>.epaisseurParois
  expr: Constraints[16] = <<sp>>.epaisseurParois
  sketch-geometry (6):
    g0: LineSegment StartX=-108.5 StartY=14.7426 StartZ=0 EndX=-112.5 EndY=14.7426 EndZ=0
    g1: LineSegment StartX=-112.5 StartY=14.7426 StartZ=0 EndX=-112.5 EndY=6.74264 EndZ=0
    g2: LineSegment StartX=-112.5 StartY=6.74264 StartZ=0 EndX=-104.5 EndY=6.74264 EndZ=0
    g3: LineSegment StartX=-104.5 StartY=6.74264 StartZ=0 EndX=-104.5 EndY=10.7426 EndZ=0
    g4: ArcOfCircle CenterX=-108.5 CenterY=10.7426 CenterZ=0 NormalX=0 NormalY=0 NormalZ=1 AngleXU=0 Radius=4 StartAngle=2e-16 EndAngle=1.5708
    g5: GeomPoint X=-115 Y=4.24264 Z=0
  constraints (17):
    c: Horizontal(g0)
    c: Coincident(g0,g1)
    c: Vertical(g1)
    c: Coincident(g1,g2)
    c: Horizontal(g2)
    c: Coincident(g2,g3)
    c: Vertical(g3)
    c: Equal(g3,g0)
    c: Equal(g2,g1)
    c: Coincident(g0,g4)
    c: DistanceX(g2,g2) = 8
    c: Tangent(g4,g3) = -1.5708
    c: DistanceX(g0,g0) = 4
    c: DistanceX(g5,g-1) = 115
    c: DistanceY(g-1,g5) = 4.24264
    c: DistanceY(g5,g1) = 2.5
    c: DistanceX(g5,g1) = 2.5
FEATURE [PartDesign::Pad] Pad006  label="padInsertFavGauch"
  AllowMultiFace = false
  BaseFeature = -> Pad005
  Direction = (1,1,1)
  Length = 10
  Length2 = 100
  Profile = -> Sketch017
  Type = 2
FEATURE [Sketcher::SketchObject] Sketch018  label="skPercageInsertFavDroit"
  FullyConstrained = true
  MapMode = 5
  Placement = pos=(0,-71,-2.13e-14) rot=(1,0,0;0.785398rad)
  Support = -> [DatumPlane007]
  expr: Constraints[0] = <<sp>>.insertDiamPercage
  expr: Constraints[1] = <<sp>>.insertFavDistAuZeroDuPLan + <<sp>>.epaisseurParois + <<sp>>.insertFAVDistBord / 2
  expr: Constraints[2] = <<sp>>.epaisseurParois + <<sp>>.insertFAVDistBord / 2
  expr: Constraints[7] = <<sp>>.largeurModuleBase - 2 * <<sp>>.epaisseurParois - <<sp>>.insertFAVDistBord
  sketch-geometry (3):
    g0: Circle CenterX=-6.5 CenterY=10.7426 CenterZ=0 NormalX=0 NormalY=0 NormalZ=1 AngleXU=0 Radius=2
    g1: Circle CenterX=-108.5 CenterY=10.7426 CenterZ=0 NormalX=0 NormalY=0 NormalZ=1 AngleXU=0 Radius=2
    g2: LineSegment StartX=-108.5 StartY=10.7426 StartZ=0 EndX=-6.5 EndY=10.7426 EndZ=0
  constraints (8):
    c: Diameter(g0) = 4
    c: DistanceY(g-1,g0) = 10.7426
    c: DistanceX(g0,g-1) = 6.5
    c: Equal(g0,g1)
    c: Coincident(g2,g1)
    c: Coincident(g2,g0)
    c: Horizontal(g2)
    c: DistanceX(g2,g2) = 102
FEATURE [PartDesign::Pocket] Pocket010  label="trouInsertFavDroit"
  AllowMultiFace = false
  BaseFeature = -> Pad006
  Length = 8
  Length2 = 100
  Profile = -> Sketch018
  Reversed = true
  Type = 0
  expr: Length = <<sp>>.insertFavProfondeur
FEATURE [PartDesign::Plane] DatumPlane011  label="planFaceAvant"
  AttachmentOffset = pos=(0,0,93.2843) rot=(-1,0,0;0.785398rad)
  Length = 168.138
  MapMode = 5
  Placement = pos=(0,-93.2843,-2.07e-14) rot=(1,0,0;0.785398rad)
  ResizeMode = 0
  Support = -> [XZ_Plane003]
  Width = 169.523
  expr: .AttachmentOffset.Base.z = <<sp>>.planFaceAvant
FEATURE [Sketcher::SketchObject] Sketch030  label="sk_rebordFav"
  FullyConstrained = true
  MapMode = 5
  Placement = pos=(0,-71,-2.13e-14) rot=(1,0,0;0.785398rad)
  Support = -> [DatumPlane007]
  expr: Constraints[0] = <<sp>>.insertFavDistAuZeroDuPLan
  expr: Constraints[20] = <<sp>>.favEpBordure
  expr: Constraints[24] = <<sp>>.Face - <<sp>>.epaisseurParois
  expr: Constraints[21] = <<sp>>.favDistBordPlan
  expr: Constraints[25] = <<sp>>.favEpBordure
  expr: Constraints[22] = <<sp>>.largeurModuleBase - 2 * <<sp>>.epaisseurParois
  expr: Constraints[19] = <<sp>>.epaisseurParois
  expr: Constraints[23] = <<sp>>.favEpBordure
  sketch-geometry (9):
    g0: GeomPoint X=0 Y=4.24264 Z=0
    g1: LineSegment StartX=-112.5 StartY=20.9853 StartZ=0 EndX=-112.5 EndY=81.7426 EndZ=0
    g2: LineSegment StartX=-112.5 StartY=81.7426 StartZ=0 EndX=-2.5 EndY=81.7426 EndZ=0
    g3: LineSegment StartX=-2.5 StartY=81.7426 StartZ=0 EndX=-2.5 EndY=20.9853 EndZ=0
    g4: LineSegment StartX=-2.5 StartY=20.9853 StartZ=0 EndX=-4 EndY=20.9853 EndZ=0
    g5: LineSegment StartX=-4 StartY=20.9853 StartZ=0 EndX=-4 EndY=80.2426 EndZ=0
    g6: LineSegment StartX=-4 StartY=80.2426 StartZ=0 EndX=-111 EndY=80.2426 EndZ=0
    g7: LineSegment StartX=-111 StartY=80.2426 StartZ=0 EndX=-111 EndY=20.9853 EndZ=0
    g8: LineSegment StartX=-111 StartY=20.9853 StartZ=0 EndX=-112.5 EndY=20.9853 EndZ=0
  constraints (26):
    c: DistanceY(g-1,g0) = 4.24264
    c: Vertical(g0,g-1)
    c: Vertical(g1)
    c: Coincident(g1,g2)
    c: Horizontal(g2)
    c: Coincident(g2,g3)
    c: Vertical(g3)
    c: Coincident(g3,g4)
    c: Horizontal(g4)
    c: Coincident(g4,g5)
    c: Vertical(g5)
    c: Coincident(g5,g6)
    c: Horizontal(g6)
    c: Coincident(g6,g7)
    c: Vertical(g7)
    c: Coincident(g7,g8)
    c: Coincident(g8,g1)
    c: Horizontal(g8)
    c: Horizontal(g7,g4)
    c: DistanceX(g3,g0) = 2.5
    c: DistanceX(g4,g4) = 1.5
    c: DistanceY(g0,g3) = 16.7426
    c: DistanceX(g1,g3) = 110
    c: DistanceY(g5,g2) = 1.5
    c: DistanceY(g0,g2) = 77.5
    c: DistanceX(g1,g7) = 1.5
FEATURE [PartDesign::Pad] Pad014  label="favRebordSupport"
  AllowMultiFace = false
  BaseFeature = -> Pocket010
  Direction = (1,1,1)
  Length = 10
  Length2 = 100
  Profile = -> Sketch030
  Type = 3
  UpToFace = -> Pocket010 [Face13]
FEATURE [PartDesign::Pad] Pad015  label="favRebord"
  AllowMultiFace = false
  BaseFeature = -> Pad014
  Direction = (1,1,1)
  Length = 4.15
  Length2 = 100
  Profile = -> Sketch030
  Reversed = true
  Type = 0
  expr: Length = <<sp>>.favBordureProf
FEATURE [Sketcher::SketchObject] Sketch031  label="sk_bourlet"
  ExternalGeometry = -> [Pad015]
  FullyConstrained = true
  MapMode = 5
  Placement = pos=(-2.5,0,0) rot=(0.57735,0.57735,0.57735;2.0944rad)
  Support = -> [Pad015]
  expr: Constraints[3] = <<sp>>.bourletMaintientRayon - <<sp>>.bourletRayonJeu
  sketch-geometry (2):
    g0: ArcOfCircle CenterX=-11.184 CenterY=55.7855 CenterZ=0 NormalX=0 NormalY=0 NormalZ=1 AngleXU=0 Radius=1.3 StartAngle=5.49779 EndAngle=8.63938
    g1: LineSegment StartX=-12.1032 StartY=56.7048 StartZ=0 EndX=-10.2647 EndY=54.8663 EndZ=0
  constraints (6):
    c: Coincident(g0,g-3)
    c: PointOnObject(g0,g-3)
    c: PointOnObject(g0,g-3)
    c: Radius(g0) = 1.3
    c: Coincident(g1,g0)
    c: Coincident(g1,g0)
FEATURE [PartDesign::Pad] Pad016  label="bourlet"
  AllowMultiFace = false
  BaseFeature = -> Pad015
  Direction = (1,1,1)
  Length = 10
  Length2 = 100
  Profile = -> Sketch031
  Reversed = true
  Type = 3
  UpToFace = -> Pad015 [Face11]
FEATURE [Sketcher::SketchObject] Sketch039
  FullyConstrained = false
  MapMode = 5
  Placement = pos=(0,-93.2843,-2.84e-14) rot=(1,0,0;0.785398rad)
  Support = -> [DatumPlane011]
  sketch-geometry (4):
    g0: LineSegment StartX=0 StartY=20.0821 StartZ=0 EndX=-90.3326 EndY=20.0821 EndZ=0
    g1: LineSegment StartX=-90.3326 StartY=20.0821 StartZ=0 EndX=-90.3326 EndY=100.134 EndZ=0
    g2: LineSegment StartX=-90.3326 StartY=100.134 StartZ=0 EndX=0 EndY=100.134 EndZ=0
    g3: LineSegment StartX=0 StartY=100.134 StartZ=0 EndX=0 EndY=20.0821 EndZ=0
  constraints (9):
    c: Coincident(g0,g1)
    c: Coincident(g1,g2)
    c: Coincident(g2,g3)
    c: Coincident(g3,g0)
    c: Horizontal(g0)
    c: Horizontal(g2)
    c: Vertical(g1)
    c: Vertical(g3)
    c: PointOnObject(g0,g-2)
FEATURE [PartDesign::Body] Body002  label="faceAvant"
  BaseFeature = -> Slice_child1
  Group = -> [Clone001,Thickness001,DatumPlane007,Sketch016,Pad005,Sketch017,Pad006,Sketch018,Pocket010,DatumPlane011,Sketch030,Pad014,Pad015,Sketch031,Pad016,Sketch039]
  Origin = -> Origin003
  Tip = -> Pad016
COMPONENT P2 — recipe-attached ("visTHCM3x6_FAV001", modeled in this document).
Construction recipe (the document's own serialized feature program — sketch geometry with constraints, then the solid features built on it; lengths are millimeters unless a unit is written):

FEATURE [Sketcher::SketchObject] Sketch034  label="Sketch"
  FullyConstrained = false
  MapMode = 5
  Support = -> [XY_Plane015]
  sketch-geometry (1):
    g0: Circle CenterX=0 CenterY=0 CenterZ=0 NormalX=0 NormalY=0 NormalZ=1 AngleXU=0 Radius=2.75
  constraints (2):
    c: Coincident(g0,g-1)
    c: Diameter(g0) = 5.5
FEATURE [PartDesign::Pad] Pad019  label="tete"
  AllowMultiFace = false
  Direction = (1,1,1)
  Length = 3
  Length2 = 100
  Profile = -> Sketch034
  Type = 0
FEATURE [Sketcher::SketchObject] Sketch001
  FullyConstrained = false
  MapMode = 5
  Placement = pos=(0,0,0) rot=(1,0,0;3.14159rad)
  Support = -> [Pad019]
  sketch-geometry (1):
    g0: Circle CenterX=0 CenterY=0 CenterZ=0 NormalX=0 NormalY=0 NormalZ=1 AngleXU=0 Radius=1.5
  constraints (2):
    c: Coincident(g0,g-1)
    c: Diameter(g0) = 3
FEATURE [PartDesign::Pad] Pad020  label="corps"
  AllowMultiFace = false
  BaseFeature = -> Pad019
  Direction = (1,1,1)
  Length = 6
  Length2 = 100
  Profile = -> Sketch001
  Type = 0
FEATURE [PartDesign::Plane] DatumPlane014
  AttachmentOffset = pos=(0,0,3) rot=(0,0,1;0rad)
  Length = 60
  MapMode = 5
  Placement = pos=(0,0,3) rot=(0,0,1;0rad)
  ResizeMode = 0
  Support = -> [XY_Plane015]
  Width = 60
FEATURE [Sketcher::SketchObject] Sketch035  label="Sketch002"
  FullyConstrained = false
  MapMode = 5
  Placement = pos=(0,0,3) rot=(0,0,1;0rad)
  Support = -> [DatumPlane014]
  sketch-geometry (7):
    g0: LineSegment StartX=0.721688 StartY=-1.25 StartZ=0 EndX=1.44338 EndY=1.0119e-12 EndZ=0
    g1: LineSegment StartX=1.44338 StartY=1.0119e-12 StartZ=0 EndX=0.721688 EndY=1.25 EndZ=0
    g2: LineSegment StartX=0.721688 StartY=1.25 StartZ=0 EndX=-0.721688 EndY=1.25 EndZ=0
    g3: LineSegment StartX=-0.721688 StartY=1.25 StartZ=0 EndX=-1.44338 EndY=8.689e-13 EndZ=0
    g4: LineSegment StartX=-1.44338 StartY=8.689e-13 StartZ=0 EndX=-0.721688 EndY=-1.25 EndZ=0
    g5: LineSegment StartX=-0.721688 StartY=-1.25 StartZ=0 EndX=0.721688 EndY=-1.25 EndZ=0
    g6: Circle CenterX=0 CenterY=0 CenterZ=0 NormalX=0 NormalY=0 NormalZ=1 AngleXU=0 Radius=1.44338
  constraints (16):
    c: Coincident(g0,g1)
    c: Coincident(g1,g2)
    c: Coincident(g2,g3)
    c: Coincident(g3,g4)
    c: Coincident(g4,g5)
    c: Coincident(g5,g0)
    c: Equal(g0, g1-g5) x5
    c: PointOnObject(g0,g6)
    c: PointOnObject(g1,g6)
    c: PointOnObject(g2,g6)
    c: PointOnObject(g3,g6)
    c: PointOnObject(g4,g6)
    c: PointOnObject(g5,g6)
    c: Coincident(g6,g-1)
    c: Horizontal(g2)
    c: DistanceY(g0,g1) = 2.5
FEATURE [PartDesign::Pocket] Pocket016  label="emprunte"
  AllowMultiFace = false
  BaseFeature = -> Pad020
  Length = 4
  Length2 = 100
  Profile = -> Sketch035
  Type = 0
FEATURE [PartDesign::Body] Body009  label="visTHCM3x6_FAV001"
  Group = -> [Sketch034,Pad019,Sketch001,Pad020,DatumPlane014,Sketch035,Pocket016]
  Origin = -> Origin019
  Placement = pos=(-6.5,-61.8718,6.01041) rot=(1,0,0;3.92699rad)
  Tip = -> Pocket016
COMPONENT P3 — recipe-attached ("visTHCM3x6_FAV002", modeled in this document).
Construction recipe (the document's own serialized feature program — sketch geometry with constraints, then the solid features built on it; lengths are millimeters unless a unit is written):

FEATURE [Sketcher::SketchObject] Sketch036
  FullyConstrained = false
  MapMode = 5
  Support = -> [XY_Plane016]
  sketch-geometry (1):
    g0: Circle CenterX=0 CenterY=0 CenterZ=0 NormalX=0 NormalY=0 NormalZ=1 AngleXU=0 Radius=2.75
  constraints (2):
    c: Coincident(g0,g-1)
    c: Diameter(g0) = 5.5
FEATURE [PartDesign::Pad] Pad021  label="tete001"
  AllowMultiFace = false
  Direction = (1,1,1)
  Length = 3
  Length2 = 100
  Profile = -> Sketch036
  Type = 0
FEATURE [Sketcher::SketchObject] Sketch037
  FullyConstrained = false
  MapMode = 5
  Placement = pos=(0,0,0) rot=(1,0,0;3.14159rad)
  Support = -> [Pad021]
  sketch-geometry (1):
    g0: Circle CenterX=0 CenterY=0 CenterZ=0 NormalX=0 NormalY=0 NormalZ=1 AngleXU=0 Radius=1.5
  constraints (2):
    c: Coincident(g0,g-1)
    c: Diameter(g0) = 3
FEATURE [PartDesign::Pad] Pad022  label="corps001"
  AllowMultiFace = false
  BaseFeature = -> Pad021
  Direction = (1,1,1)
  Length = 6
  Length2 = 100
  Profile = -> Sketch037
  Type = 0
FEATURE [PartDesign::Plane] DatumPlane015
  AttachmentOffset = pos=(0,0,3) rot=(0,0,1;0rad)
  Length = 60
  MapMode = 5
  Placement = pos=(0,0,3) rot=(0,0,1;0rad)
  ResizeMode = 0
  Support = -> [XY_Plane016]
  Width = 60
FEATURE [Sketcher::SketchObject] Sketch038
  FullyConstrained = false
  MapMode = 5
  Placement = pos=(0,0,3) rot=(0,0,1;0rad)
  Support = -> [DatumPlane015]
  sketch-geometry (7):
    g0: LineSegment StartX=0.721688 StartY=-1.25 StartZ=0 EndX=1.44338 EndY=1.0119e-12 EndZ=0
    g1: LineSegment StartX=1.44338 StartY=1.0119e-12 StartZ=0 EndX=0.721688 EndY=1.25 EndZ=0
    g2: LineSegment StartX=0.721688 StartY=1.25 StartZ=0 EndX=-0.721688 EndY=1.25 EndZ=0
    g3: LineSegment StartX=-0.721688 StartY=1.25 StartZ=0 EndX=-1.44338 EndY=8.689e-13 EndZ=0
    g4: LineSegment StartX=-1.44338 StartY=8.689e-13 StartZ=0 EndX=-0.721688 EndY=-1.25 EndZ=0
    g5: LineSegment StartX=-0.721688 StartY=-1.25 StartZ=0 EndX=0.721688 EndY=-1.25 EndZ=0
    g6: Circle CenterX=0 CenterY=0 CenterZ=0 NormalX=0 NormalY=0 NormalZ=1 AngleXU=0 Radius=1.44338
  constraints (16):
    c: Coincident(g0,g1)
    c: Coincident(g1,g2)
    c: Coincident(g2,g3)
    c: Coincident(g3,g4)
    c: Coincident(g4,g5)
    c: Coincident(g5,g0)
    c: Equal(g0, g1-g5) x5
    c: PointOnObject(g0,g6)
    c: PointOnObject(g1,g6)
    c: PointOnObject(g2,g6)
    c: PointOnObject(g3,g6)
    c: PointOnObject(g4,g6)
    c: PointOnObject(g5,g6)
    c: Coincident(g6,g-1)
    c: Horizontal(g2)
    c: DistanceY(g0,g1) = 2.5
FEATURE [PartDesign::Pocket] Pocket017  label="emprunte001"
  AllowMultiFace = false
  BaseFeature = -> Pad022
  Length = 4
  Length2 = 100
  Profile = -> Sketch038
  Type = 0
FEATURE [PartDesign::Body] Body010  label="visTHCM3x6_FAV002"
  Group = -> [Sketch036,Pad021,Sketch037,Pad022,DatumPlane015,Sketch038,Pocket017]
  Origin = -> Origin020
  Placement = pos=(-28.5,-61.8718,6.01041) rot=(1,0,0;3.92699rad)
  Tip = -> Pocket017
COMPONENT P4 — recipe-attached ("ecranLCD20x2I2X", modeled in this document).
Construction recipe (the document's own serialized feature program — sketch geometry with constraints, then the solid features built on it; lengths are millimeters unless a unit is written):

FEATURE [Sketcher::SketchObject] Sketch  label="profileDeBase"
  FullyConstrained = true
  MapMode = 5
  Placement = pos=(0,0,0) rot=(0.57735,0.57735,0.57735;2.0944rad)
  Support = -> [YZ_Plane001]
  expr: Constraints[8] = <<sp>>.Base
  expr: Constraints[9] = <<sp>>.anglePetitRetourBase
  expr: Constraints[10] = <<sp>>.petitRetour
  expr: Constraints[11] = <<sp>>.angleFacePetitRetour
  expr: Constraints[12] = <<sp>>.Face
  expr: Constraints[13] = <<sp>>.angleFaceRetourHaut
  sketch-geometry (5):
    g0: LineSegment StartX=0 StartY=0 StartZ=0 EndX=-65 EndY=0 EndZ=0
    g1: LineSegment StartX=-65 StartY=0 StartZ=0 EndX=-79.1421 EndY=14.1421 EndZ=0
    g2: LineSegment StartX=-79.1421 StartY=14.1421 StartZ=0 EndX=-22.5736 EndY=70.7107 EndZ=0
    g3: LineSegment StartX=-22.5736 StartY=70.7107 StartZ=0 EndX=0 EndY=48.1371 EndZ=0
    g4: LineSegment StartX=0 StartY=48.1371 StartZ=0 EndX=0 EndY=0 EndZ=0
  constraints (14):
    c: Coincident(g-1,g0)
    c: Horizontal(g0)
    c: Coincident(g0,g1)
    c: Coincident(g1,g2)
    c: Coincident(g2,g3)
    c: PointOnObject(g3,g-2)
    c: Coincident(g3,g4)
    c: Coincident(g4,g0)
    c: DistanceX(g0,g0) = 65
    c: Angle(g0,g1) = 2.35619
    c: Distance(g1) = 20
    c: Angle(g1,g2) = 1.5708
    c: Distance(g2) = 80
    c: Angle(g2,g3) = 1.5708
FEATURE [PartDesign::Pad] Pad
  AllowMultiFace = false
  Direction = (1,1,1)
  Length = 115
  Length2 = 100
  Placement = pos=(0,0,0) rot=(0.57735,0.57735,0.57735;2.0944rad)
  Profile = -> Sketch
  Reversed = true
  Type = 0
  expr: Length = <<sp>>.largeurModuleBase
FEATURE [PartDesign::Plane] DatumPlane
  AttachmentOffset = pos=(71,0,0) rot=(0,-1,0;0.785398rad)
  Length = 98.6412
  MapMode = 5
  Placement = pos=(-7.9e-15,8e-15,71) rot=(0.678598,0.678598,0.281085;3.68962rad)
  ResizeMode = 0
  Support = -> [Pad]
  Width = 63.0813
FEATURE [PartDesign::Body] Body  label="Base"
  Group = -> [Sketch,Pad,DatumPlane]
  Origin = -> Origin001
  Tip = -> Pad
COMPONENT P5 — geometry summary ("xt60fem"; no construction recipe available for this part):
  bounding box: 20.5 x 16.5 x 7.5 mm
  tessellated surface: 23,200 triangles
  volume: 955 mm^3 (38% of its bounding box)
COMPONENT P6 — geometry summary ("xt60Male"; no construction recipe available for this part):
  bounding box: 20.2 x 16.6 x 7.5 mm
  tessellated surface: 14,480 triangles
  volume: 1201 mm^3 (48% of its bounding box)
COMPONENT P7 — geometry summary ("ZSB_RUTHEX_M3_5.7_001"; no construction recipe available for this part):
  bounding box: 5.7 x 4.6 x 4.6 mm
  tessellated surface: 4,640 triangles
  volume: 44 mm^3 (36% of its bounding box)
  symmetry: revolution-symmetric about the y axis through its bounding-box center; mirror-symmetric across its x mid-plane, z mid-plane
COMPONENT P8 — geometry summary ("ZSB_RUTHEX_M3_5.7_002"; no construction recipe available for this part):
  bounding box: 5.7 x 4.6 x 4.6 mm
  tessellated surface: 4,640 triangles
  volume: 44 mm^3 (36% of its bounding box)
  symmetry: revolution-symmetric about the y axis through its bounding-box center; mirror-symmetric across its x mid-plane, z mid-plane
COMPONENT P9 — geometry summary ("ZSB_RUTHEX_M3_5.7_003"; no construction recipe available for this part):
  bounding box: 6.9 x 6.9 x 4.6 mm
  tessellated surface: 4,640 triangles
  volume: 44 mm^3 (20% of its bounding box)
  symmetry: mirror-symmetric across its x mid-plane
COMPONENT P10 — geometry summary ("ZSB_RUTHEX_M3_5.7_004"; no construction recipe available for this part):
  bounding box: 6.9 x 6.9 x 4.6 mm
  tessellated surface: 4,640 triangles
  volume: 44 mm^3 (20% of its bounding box)
  symmetry: mirror-symmetric across its x mid-plane
COMPONENT P11 — recipe-attached ("partVisPointeauM3x10_001", modeled in this document).
Construction recipe (the document's own serialized feature program — sketch geometry with constraints, then the solid features built on it; lengths are millimeters unless a unit is written):

FEATURE [Sketcher::SketchObject] Sketch025
  FullyConstrained = false
  MapMode = 5
  Support = -> [XY_Plane008]
  sketch-geometry (1):
    g0: Circle CenterX=0 CenterY=0 CenterZ=0 NormalX=0 NormalY=0 NormalZ=1 AngleXU=0 Radius=1.5
  constraints (2):
    c: Coincident(g0,g-1)
    c: Diameter(g0) = 3
FEATURE [Sketcher::SketchObject] Sketch026
  FullyConstrained = false
  MapMode = 5
  Support = -> [XY_Plane008]
  sketch-geometry (7):
    g0: LineSegment StartX=0.433013 StartY=-0.75 StartZ=0 EndX=0.866025 EndY=1.25568e-11 EndZ=0
    g1: LineSegment StartX=0.866025 StartY=1.25568e-11 StartZ=0 EndX=0.433013 EndY=0.75 EndZ=0
    g2: LineSegment StartX=0.433013 StartY=0.75 StartZ=0 EndX=-0.433013 EndY=0.75 EndZ=0
    g3: LineSegment StartX=-0.433013 StartY=0.75 StartZ=0 EndX=-0.866025 EndY=2.91366e-11 EndZ=0
    g4: LineSegment StartX=-0.866025 StartY=2.91366e-11 StartZ=0 EndX=-0.433013 EndY=-0.75 EndZ=0
    g5: LineSegment StartX=-0.433013 StartY=-0.75 StartZ=0 EndX=0.433013 EndY=-0.75 EndZ=0
    g6: Circle CenterX=0 CenterY=0 CenterZ=0 NormalX=0 NormalY=0 NormalZ=1 AngleXU=0 Radius=0.866025
  constraints (16):
    c: Coincident(g0,g1)
    c: Coincident(g1,g2)
    c: Coincident(g2,g3)
    c: Coincident(g3,g4)
    c: Coincident(g4,g5)
    c: Coincident(g5,g0)
    c: Equal(g0, g1-g5) x5
    c: PointOnObject(g0,g6)
    c: PointOnObject(g1,g6)
    c: PointOnObject(g2,g6)
    c: PointOnObject(g3,g6)
    c: PointOnObject(g4,g6)
    c: PointOnObject(g5,g6)
    c: Coincident(g6,g-1)
    c: Horizontal(g2)
    c: DistanceY(g0,g1) = 1.5
FEATURE [PartDesign::Pad] Pad012
  AllowMultiFace = false
  Direction = (1,1,1)
  Length = 10
  Length2 = 100
  Profile = -> Sketch025
  Type = 0
FEATURE [PartDesign::Chamfer] Chamfer
  Angle = 45
  Base = -> Pad012 [Edge3]
  BaseFeature = -> Pad012
  ChamferType = 0
  FlipDirection = false
  Size = 1.4
  Size2 = 1
  SupportTransform = false
FEATURE [PartDesign::Pocket] Pocket013
  AllowMultiFace = false
  BaseFeature = -> Chamfer
  Length = 1.5
  Length2 = 100
  Profile = -> Sketch026
  Reversed = true
  Type = 0
FEATURE [PartDesign::Chamfer] Chamfer001
  Angle = 45
  Base = -> Pocket013 [Edge3]
  BaseFeature = -> Pocket013
  ChamferType = 0
  FlipDirection = false
  Size = 0.1
  Size2 = 1
  SupportTransform = false
FEATURE [PartDesign::Body] Body005  label="bodyVisPointeauM3x10_001"
  Group = -> [Sketch025,Pad012,Chamfer,Sketch026,Pocket013,Chamfer001]
  Origin = -> Origin013
  Tip = -> Chamfer001
COMPONENT P12 — recipe-attached ("partVisPointeauM3x10_002", modeled in this document).
Construction recipe (the document's own serialized feature program — sketch geometry with constraints, then the solid features built on it; lengths are millimeters unless a unit is written):

FEATURE [Sketcher::SketchObject] Sketch027
  FullyConstrained = false
  MapMode = 5
  Support = -> [XY_Plane010]
  sketch-geometry (7):
    g0: LineSegment StartX=0.433013 StartY=-0.75 StartZ=0 EndX=0.866025 EndY=1.25568e-11 EndZ=0
    g1: LineSegment StartX=0.866025 StartY=1.25568e-11 StartZ=0 EndX=0.433013 EndY=0.75 EndZ=0
    g2: LineSegment StartX=0.433013 StartY=0.75 StartZ=0 EndX=-0.433013 EndY=0.75 EndZ=0
    g3: LineSegment StartX=-0.433013 StartY=0.75 StartZ=0 EndX=-0.866025 EndY=2.91366e-11 EndZ=0
    g4: LineSegment StartX=-0.866025 StartY=2.91366e-11 StartZ=0 EndX=-0.433013 EndY=-0.75 EndZ=0
    g5: LineSegment StartX=-0.433013 StartY=-0.75 StartZ=0 EndX=0.433013 EndY=-0.75 EndZ=0
    g6: Circle CenterX=0 CenterY=0 CenterZ=0 NormalX=0 NormalY=0 NormalZ=1 AngleXU=0 Radius=0.866025
  constraints (16):
    c: Coincident(g0,g1)
    c: Coincident(g1,g2)
    c: Coincident(g2,g3)
    c: Coincident(g3,g4)
    c: Coincident(g4,g5)
    c: Coincident(g5,g0)
    c: Equal(g0, g1-g5) x5
    c: PointOnObject(g0,g6)
    c: PointOnObject(g1,g6)
    c: PointOnObject(g2,g6)
    c: PointOnObject(g3,g6)
    c: PointOnObject(g4,g6)
    c: PointOnObject(g5,g6)
    c: Coincident(g6,g-1)
    c: Horizontal(g2)
    c: DistanceY(g0,g1) = 1.5
FEATURE [Sketcher::SketchObject] Sketch028
  FullyConstrained = false
  MapMode = 5
  Support = -> [XY_Plane010]
  sketch-geometry (1):
    g0: Circle CenterX=0 CenterY=0 CenterZ=0 NormalX=0 NormalY=0 NormalZ=1 AngleXU=0 Radius=1.5
  constraints (2):
    c: Coincident(g0,g-1)
    c: Diameter(g0) = 3
FEATURE [PartDesign::Pad] Pad013
  AllowMultiFace = false
  Direction = (1,1,1)
  Length = 10
  Length2 = 100
  Profile = -> Sketch028
  Type = 0
FEATURE [PartDesign::Chamfer] Chamfer003
  Angle = 45
  Base = -> Pad013 [Edge3]
  BaseFeature = -> Pad013
  ChamferType = 0
  FlipDirection = false
  Size = 1.4
  Size2 = 1
  SupportTransform = false
FEATURE [PartDesign::Pocket] Pocket014
  AllowMultiFace = false
  BaseFeature = -> Chamfer003
  Length = 1.5
  Length2 = 100
  Profile = -> Sketch027
  Reversed = true
  Type = 0
FEATURE [PartDesign::Chamfer] Chamfer002
  Angle = 45
  Base = -> Pocket014 [Edge3]
  BaseFeature = -> Pocket014
  ChamferType = 0
  FlipDirection = false
  Size = 0.1
  Size2 = 1
  SupportTransform = false
FEATURE [PartDesign::Body] Body006  label="bodyVisPointeauM3x10_002"
  Group = -> [Sketch028,Pad013,Chamfer003,Sketch027,Pocket014,Chamfer002]
  Origin = -> Origin015
  Tip = -> Chamfer002
COMPONENT P13 — recipe-attached ("tigeLaiton001", modeled in this document).
Construction recipe (the document's own serialized feature program — sketch geometry with constraints, then the solid features built on it; lengths are millimeters unless a unit is written):

FEATURE [PartDesign::Plane] DatumPlane012  label="planBaseTige"
  AttachmentOffset = pos=(0,0,-5.18) rot=(0,0,1;0rad)
  Length = 60
  MapMode = 5
  Placement = pos=(-5.18,1.2e-15,-1.2e-15) rot=(0.57735,0.57735,0.57735;2.0944rad)
  ResizeMode = 0
  Support = -> [YZ_Plane012]
  Width = 60
  expr: .AttachmentOffset.Base.z = -<<tige>>.planBaseTigeposX
FEATURE [Sketcher::SketchObject] Sketch032  label="sk_tiges"
  FullyConstrained = true
  MapMode = 5
  Placement = pos=(-5.18,1.2e-15,-1.2e-15) rot=(0.57735,0.57735,0.57735;2.0944rad)
  Support = -> [DatumPlane012]
  expr: Constraints[0] = <<tige>>.tigeDiam
  expr: Constraints[1] = <<tige>>.tigePosY
  expr: Constraints[2] = <<tige>>.tigePosX
  sketch-geometry (1):
    g0: Circle CenterX=-14 CenterY=14.3 CenterZ=0 NormalX=0 NormalY=0 NormalZ=1 AngleXU=0 Radius=1.25
  constraints (3):
    c: Diameter(g0) = 2.5
    c: DistanceY(g-1,g0) = 14.3
    c: DistanceX(g0,g-1) = 14
FEATURE [PartDesign::Pad] Pad017  label="tigeBasse"
  AllowMultiFace = false
  Direction = (1,1,1)
  Length = 98.62
  Length2 = 100
  Placement = pos=(-5.18,1e-15,-1e-15) rot=(0.57735,0.57735,0.57735;2.0944rad)
  Profile = -> Sketch032
  Reversed = true
  Type = 0
  expr: Length = <<tige>>.tigeLong
FEATURE [PartDesign::Body] Body007  label="tigeLaiton"
  Group = -> [DatumPlane012,Sketch032,Pad017]
  Origin = -> Origin016
  Tip = -> Pad017
FEATURE [PartDesign::Plane] DatumPlane013  label="planTige2"
  AttachmentOffset = pos=(0,0,-5.18) rot=(0,0,1;0rad)
  Length = 60
  MapMode = 5
  Placement = pos=(-5.18,1.2e-15,-1.2e-15) rot=(0.57735,0.57735,0.57735;2.0944rad)
  ResizeMode = 0
  Support = -> [YZ_Plane014]
  Width = 60
  expr: .AttachmentOffset.Base.z = -<<tige>>.planBaseTigeposX
FEATURE [Sketcher::SketchObject] Sketch033  label="sk_tige2"
  FullyConstrained = true
  MapMode = 5
  Placement = pos=(-5.18,1.2e-15,-1.2e-15) rot=(0.57735,0.57735,0.57735;2.0944rad)
  Support = -> [DatumPlane013]
  expr: Constraints[0] = <<tige>>.tigeDiam
  expr: Constraints[1] = <<tige>>.tigePosX
  expr: Constraints[2] = <<tige>>.tigePosY + <<tige>>.xtEcartBroches
  sketch-geometry (1):
    g0: Circle CenterX=-14 CenterY=21.86 CenterZ=0 NormalX=0 NormalY=0 NormalZ=1 AngleXU=0 Radius=1.25
  constraints (3):
    c: Diameter(g0) = 2.5
    c: DistanceX(g0,g-1) = 14
    c: DistanceY(g-1,g0) = 21.86
FEATURE [PartDesign::Pad] Pad018
  AllowMultiFace = false
  Direction = (1,1,1)
  Length = 98.62
  Length2 = 100
  Placement = pos=(-5.18,1e-15,-1e-15) rot=(0.57735,0.57735,0.57735;2.0944rad)
  Profile = -> Sketch033
  Reversed = true
  Type = 0
  expr: Length = <<tige>>.tigeLong
FEATURE [PartDesign::Body] Body008  label="tige2"
  Group = -> [DatumPlane013,Sketch033,Pad018]
  Origin = -> Origin018
  Tip = -> Pad018
COMPONENT P14 — recipe-attached ("BNC_embase", modeled in this document).
Construction recipe (the document's own serialized feature program — sketch geometry with constraints, then the solid features built on it; lengths are millimeters unless a unit is written):

FEATURE [Sketcher::SketchObject] Sketch040  label="sk_trou"
  FullyConstrained = true
  MapMode = 5
  Support = -> [XY_Plane041]
  expr: Constraints[5] = <<bnc>>.trouMeplatDepuisLeCentre + <<bnc>>.trouJeu
  expr: Constraints[1] = <<bnc>>.trouDiam + <<bnc>>.trouJeu
  sketch-geometry (2):
    g0: ArcOfCircle CenterX=0 CenterY=0 CenterZ=0 NormalX=0 NormalY=0 NormalZ=1 AngleXU=0 Radius=5.15 StartAngle=0.696659 EndAngle=5.58653
    g1: LineSegment StartX=3.95 StartY=3.30454 StartZ=0 EndX=3.95 EndY=-3.30454 EndZ=0
  constraints (6):
    c: Coincident(g0,g-1)
    c: Diameter(g0) = 10.3
    c: Vertical(g1)
    c: Coincident(g0,g1)
    c: Coincident(g0,g1)
    c: DistanceX(g0,g0) = 3.95
FEATURE [PartDesign::Body] Body011  label="bncBodyPourTrou"
  Group = -> [Sketch040]
  Origin = -> Origin041
COMPONENT P15 — recipe-attached ("DCDCLM2596", modeled in this document).
Construction recipe (the document's own serialized feature program — sketch geometry with constraints, then the solid features built on it; lengths are millimeters unless a unit is written):

FEATURE [PartDesign::Plane] DatumPlane016
  AttachmentOffset = pos=(0,0,-3) rot=(0,0,1;0rad)
  Length = 60
  MapMode = 5
  Placement = pos=(0,3,7e-16) rot=(1,0,0;1.5708rad)
  ResizeMode = 0
  Support = -> [XZ_Plane043]
  Width = 60
FEATURE [Sketcher::SketchObject] Sketch041
  FullyConstrained = false
  MapMode = 5
  Placement = pos=(0,3,7e-16) rot=(1,0,0;1.5708rad)
  Support = -> [DatumPlane016]
  sketch-geometry (2):
    g0: Circle CenterX=36.7561 CenterY=-2.5011 CenterZ=0 NormalX=0 NormalY=0 NormalZ=1 AngleXU=0 Radius=1.5
    g1: Circle CenterX=6.49609 CenterY=-19.2611 CenterZ=0 NormalX=0 NormalY=0 NormalZ=1 AngleXU=0 Radius=1.5
  constraints (4):
    c: Diameter(g1) = 3
    c: Equal(g0,g1)
    c: DistanceX(g1,g0) = 30.26
    c: DistanceY(g1,g0) = 16.76
FEATURE [PartDesign::Body] Body012  label="Body"
  Group = -> [DatumPlane016,Sketch041]
  Origin = -> Origin043
COMPONENT P16 — geometry summary ("switch"; no construction recipe available for this part):
  bounding box: 38.3 x 33.1 x 13.9 mm
  tessellated surface: 4,352 triangles
  volume: 6127 mm^3 (35% of its bounding box)
PROVENANCE & LICENSES
A FreeCAD (.FCStd) document from a public repository crawl; recipes are the document's own serialized feature recipes (and, for linked parts, companion documents' recipes).
License: as declared in the source repository (recorded in the dataset sidecar).
